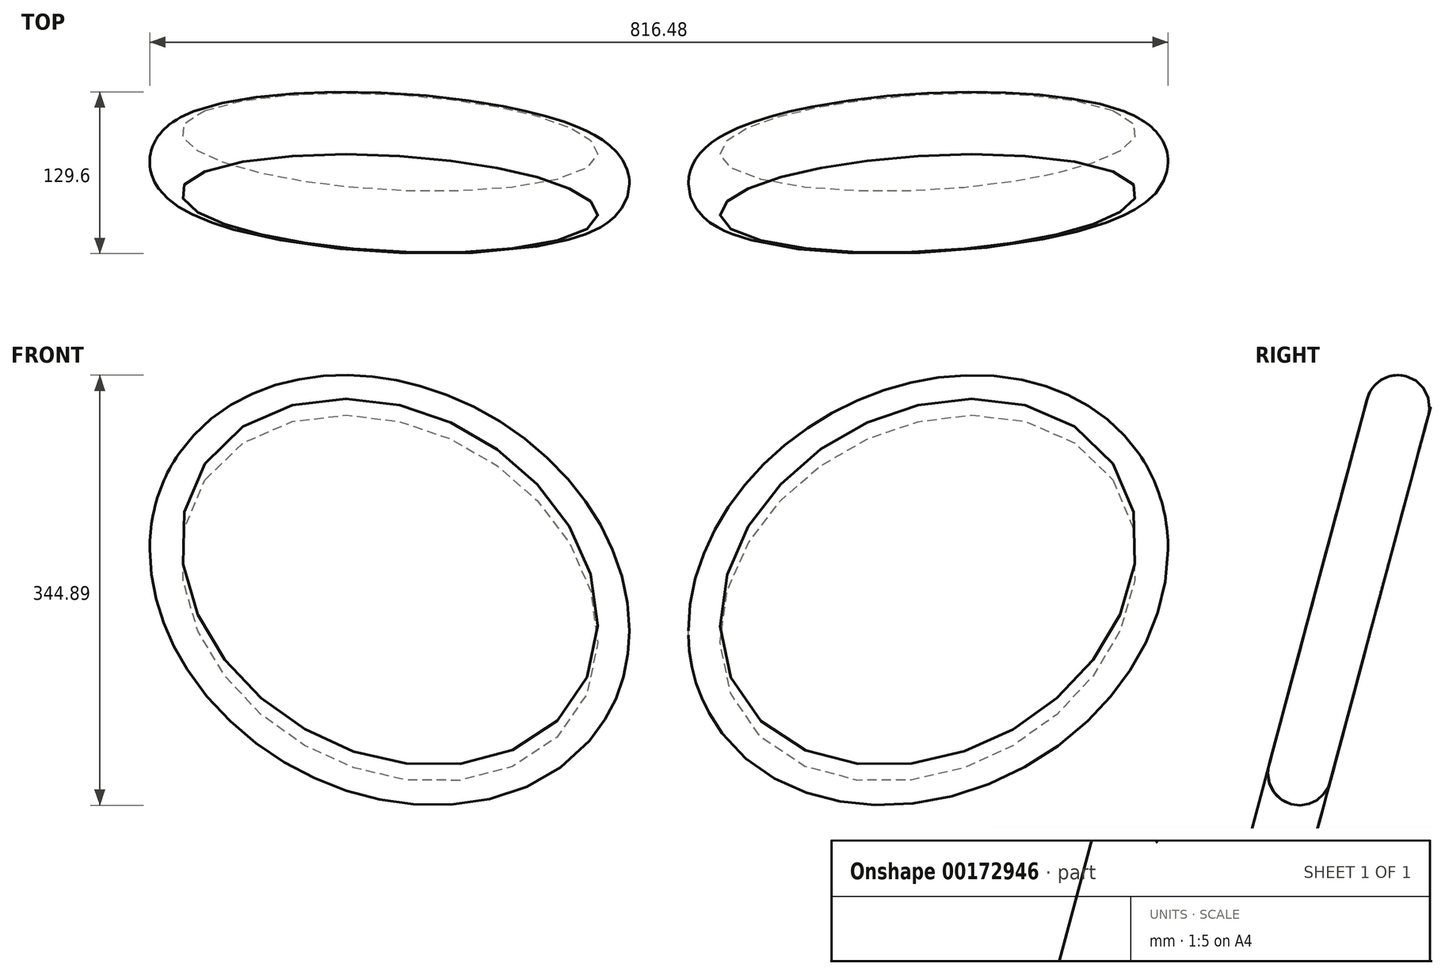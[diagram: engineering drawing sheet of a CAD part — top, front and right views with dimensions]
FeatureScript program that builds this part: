
annotation { "Feature Type Name" : "Feature", "Feature Type Description" : "" }
export const myFeature = defineFeature(function(context is Context, id is Id, definition is map)
    precondition{}
    {
        {
            var Q0;
            Q0=qCreatedBy(makeId("Top.planeOp"),FACE);
            var sketch = newSketch(context, id + "F0", { "sketchPlane" : qUnion([Q0])});
            skLineSegment(sketch, "E0", {"start": v(-75.84, 0) * mm, "end": v(76.2, 0) * mm, "construction": true});
            skSolve(sketch);
        }
        {
            var Q0;
            Q0=sQuery(id+"F0.wireOp",EDGE,"E0");
            cPlane(context, id + "F1", {"entities" : qUnion([Q0]), "cplaneType" : CPlaneType.LINE_ANGLE, "offset" : 25.4 * mm, "angle" : 345 * degree, "width" : 152.4 * mm, "height" : 152.4 * mm});
        }
        {
            var Q0;
            Q0=qCreatedBy(id+"F1.planeOp",FACE);
            var sketch = newSketch(context, id + "F2", { "sketchPlane" : qUnion([Q0])});
            skEllipse(sketch, "E1", {"center": v(-26.57, 14.14) * mm, "majorRadius": 203.2 * mm, "minorRadius": 165.1 * mm, "majorAxis": v(0.83, 0.55)});
            skLineSegment(sketch, "E2", {"start": v(-242.47, 115.68) * mm, "end": v(-242.47, -89.53) * mm, "construction": true});
            skEllipse(sketch, "E3.MirrorC", {"center": v(-458.37, 14.14) * mm, "majorRadius": 203.2 * mm, "minorRadius": 165.1 * mm, "majorAxis": v(-0.83, 0.55)});
            skSolve(sketch);
        }
        {
            var Q0;
            Q0=makeQuery(id+"F2.imprint","IMPRINT",FACE,{"disambiguationData":[TD([[makeQuery(id+"F2.imprint","IMPRINT",EDGE,{"derivedFrom":sQuery(id+"F2.wireOp",EDGE,"E1")}),1.0]])]});
            var Q1;
            Q1=makeQuery(id+"F2.imprint","IMPRINT",FACE,{"disambiguationData":[TD([[makeQuery(id+"F2.imprint","IMPRINT",EDGE,{"derivedFrom":sQuery(id+"F2.wireOp",EDGE,"E3.MirrorC")}),1.0]])]});
            extrude(context, id + "F3", {"entities" : qUnion([Q0, Q1]), "endBound" : BoundingType.SYMMETRIC, "depth" : 50.8 * mm});
        }
        {
            var Q0;
            Q0=makeQuery(id+"F3.opExtrude","CAP_EDGE",EDGE,{"disambiguationData":[OSD([sQuery(id+"F2.wireOp",EDGE,"E1")])],"isStart":true});
            var Q1;
            Q1=makeQuery(id+"F3.opExtrude","CAP_EDGE",EDGE,{"disambiguationData":[OSD([sQuery(id+"F2.wireOp",EDGE,"E1")])],"isStart":false});
            var Q2;
            Q2=makeQuery(id+"F3.opExtrude","CAP_EDGE",EDGE,{"disambiguationData":[OSD([sQuery(id+"F2.wireOp",EDGE,"E3.MirrorC")])],"isStart":true});
            var Q3;
            Q3=makeQuery(id+"F3.opExtrude","CAP_EDGE",EDGE,{"disambiguationData":[OSD([sQuery(id+"F2.wireOp",EDGE,"E3.MirrorC")])],"isStart":false});
            fillet(context, id + "F4", {"entities" : qUnion([Q0, Q1, Q2, Q3]), "radius" : 25.4 * mm, "tangentPropagation" : true, "allowEdgeOverflow" : false});
        }
    });
